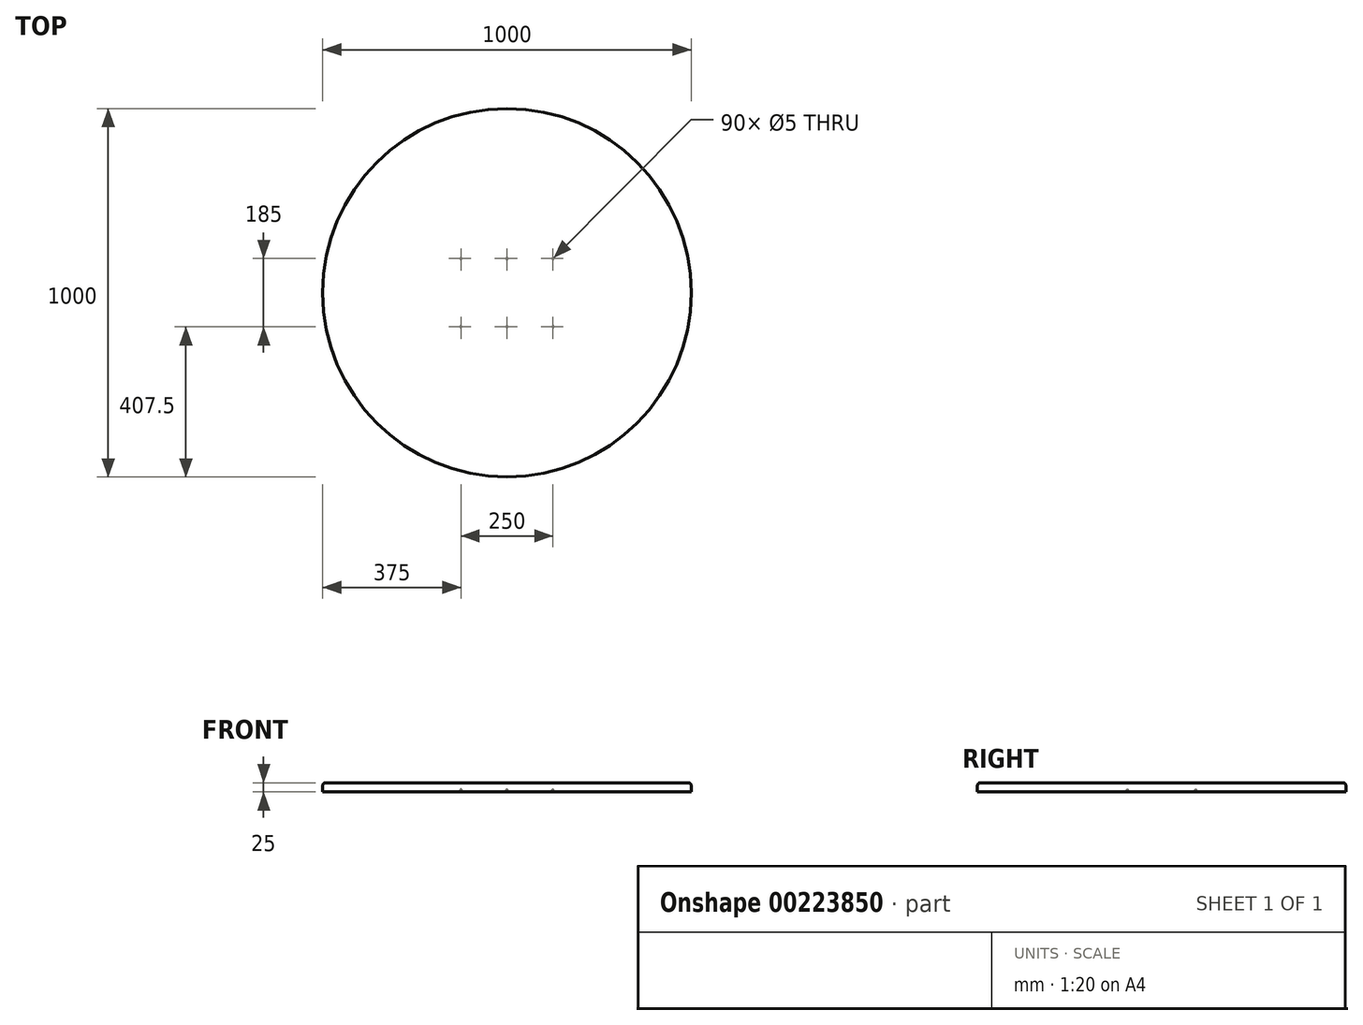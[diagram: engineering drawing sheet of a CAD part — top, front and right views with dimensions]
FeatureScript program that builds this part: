
annotation { "Feature Type Name" : "Feature", "Feature Type Description" : "" }
export const myFeature = defineFeature(function(context is Context, id is Id, definition is map)
    precondition{}
    {
        {
            var Q0;
            Q0=qCreatedBy(makeId("Top.planeOp"),FACE);
            var sketch = newSketch(context, id + "F0", { "sketchPlane" : qUnion([Q0])});
            skCircle(sketch, "E0", {"center": v(0, 0) * mm, "radius": 500 * mm});
            skSolve(sketch);
        }
        {
            var Q0;
            Q0=makeQuery(id+"F0.imprint","IMPRINT",FACE,{"disambiguationData":[TD([[makeQuery(id+"F0.imprint","IMPRINT",EDGE,{"derivedFrom":sQuery(id+"F0.wireOp",EDGE,"E0")}),1.0]])]});
            extrude(context, id + "F1", {"entities" : qUnion([Q0]), "oppositeDirection" : true, "depth" : 25 * mm});
        }
        {
            var Q0;
            Q0=makeQuery(id+"F1.opExtrude","CAP_FACE",FACE,{"disambiguationData":[OSD([sQuery(id+"F0.wireOp",EDGE,"E0")])],"isStart":true});
            fillet(context, id + "F2", {"entities" : qUnion([Q0]), "radius" : 8 * mm, "tangentPropagation" : true, "allowEdgeOverflow" : false});
        }
        {
            var Q0;
            Q0=makeQuery(id+"F1.opExtrude","CAP_FACE",FACE,{"disambiguationData":[OSD([sQuery(id+"F0.wireOp",EDGE,"E0")])],"isStart":false});
            var sketch = newSketch(context, id + "F3", { "sketchPlane" : qUnion([Q0])});
            skLineSegment(sketch, "E1.bottom", {"start": v(142.5, 107.5) * mm, "end": v(-142.5, 107.5) * mm});
            skLineSegment(sketch, "E1.top", {"start": v(142.5, -107.5) * mm, "end": v(-142.5, -107.5) * mm});
            skLineSegment(sketch, "E1.left", {"start": v(142.5, 107.5) * mm, "end": v(142.5, -107.5) * mm});
            skLineSegment(sketch, "E1.right", {"start": v(-142.5, 107.5) * mm, "end": v(-142.5, -107.5) * mm});
            skPoint(sketch, "E1.middle", {"position": v(0, 0) * mm});
            skLineSegment(sketch, "E2.bottom", {"start": v(125, 92.5) * mm, "end": v(-125, 92.5) * mm});
            skLineSegment(sketch, "E2.top", {"start": v(125, -92.5) * mm, "end": v(-125, -92.5) * mm});
            skLineSegment(sketch, "E2.left", {"start": v(125, 92.5) * mm, "end": v(125, -92.5) * mm});
            skLineSegment(sketch, "E2.right", {"start": v(-125, 92.5) * mm, "end": v(-125, -92.5) * mm});
            skLineSegment(sketch, "E3", {"start": v(0, 92.5) * mm, "end": v(0, -92.5) * mm});
            skCircle(sketch, "E4", {"center": v(125, 92.5) * mm, "radius": 2.5 * mm});
            skCircle(sketch, "E5", {"center": v(0, 92.5) * mm, "radius": 2.5 * mm});
            skCircle(sketch, "E6", {"center": v(-125, 92.5) * mm, "radius": 2.5 * mm});
            skCircle(sketch, "E7", {"center": v(-125, -92.5) * mm, "radius": 2.5 * mm});
            skCircle(sketch, "E8", {"center": v(0, -92.5) * mm, "radius": 2.5 * mm});
            skCircle(sketch, "E9", {"center": v(125, -92.5) * mm, "radius": 2.5 * mm});
            skSolve(sketch);
        }
        {
            var Q0;
            Q0=sQuery(id+"F3.wireOp",VERTEX,"E2.right.start");
            var Q1;
            Q1=sQuery(id+"F3.wireOp",VERTEX,"E8.center");
            var Q2;
            Q2=sQuery(id+"F3.wireOp",VERTEX,"E9.center");
            var Q3;
            Q3=sQuery(id+"F3.wireOp",VERTEX,"E4.center");
            var Q4;
            Q4=sQuery(id+"F3.wireOp",VERTEX,"E7.center");
            var Q5;
            Q5=sQuery(id+"F3.wireOp",VERTEX,"E3.start");
            var Q6;
            Q6=makeQuery(id+"F1.opExtrude","SWEPT_BODY",BODY,{"disambiguationData":[OSD([sQuery(id+"F0.wireOp",EDGE,"E0")])]});
            hole(context, id + "F4", {"style" : HoleStyle.SIMPLE, "endStyle" : HoleEndStyle.BLIND, "holeDiameter" : 5 * mm, "holeDepth" : 6 * mm, "locations" : qUnion([Q0, Q1, Q2, Q3, Q4, Q5]), "scope" : qUnion([Q6]), "startStyle" : HoleStartStyle.PART});
        }
    });
